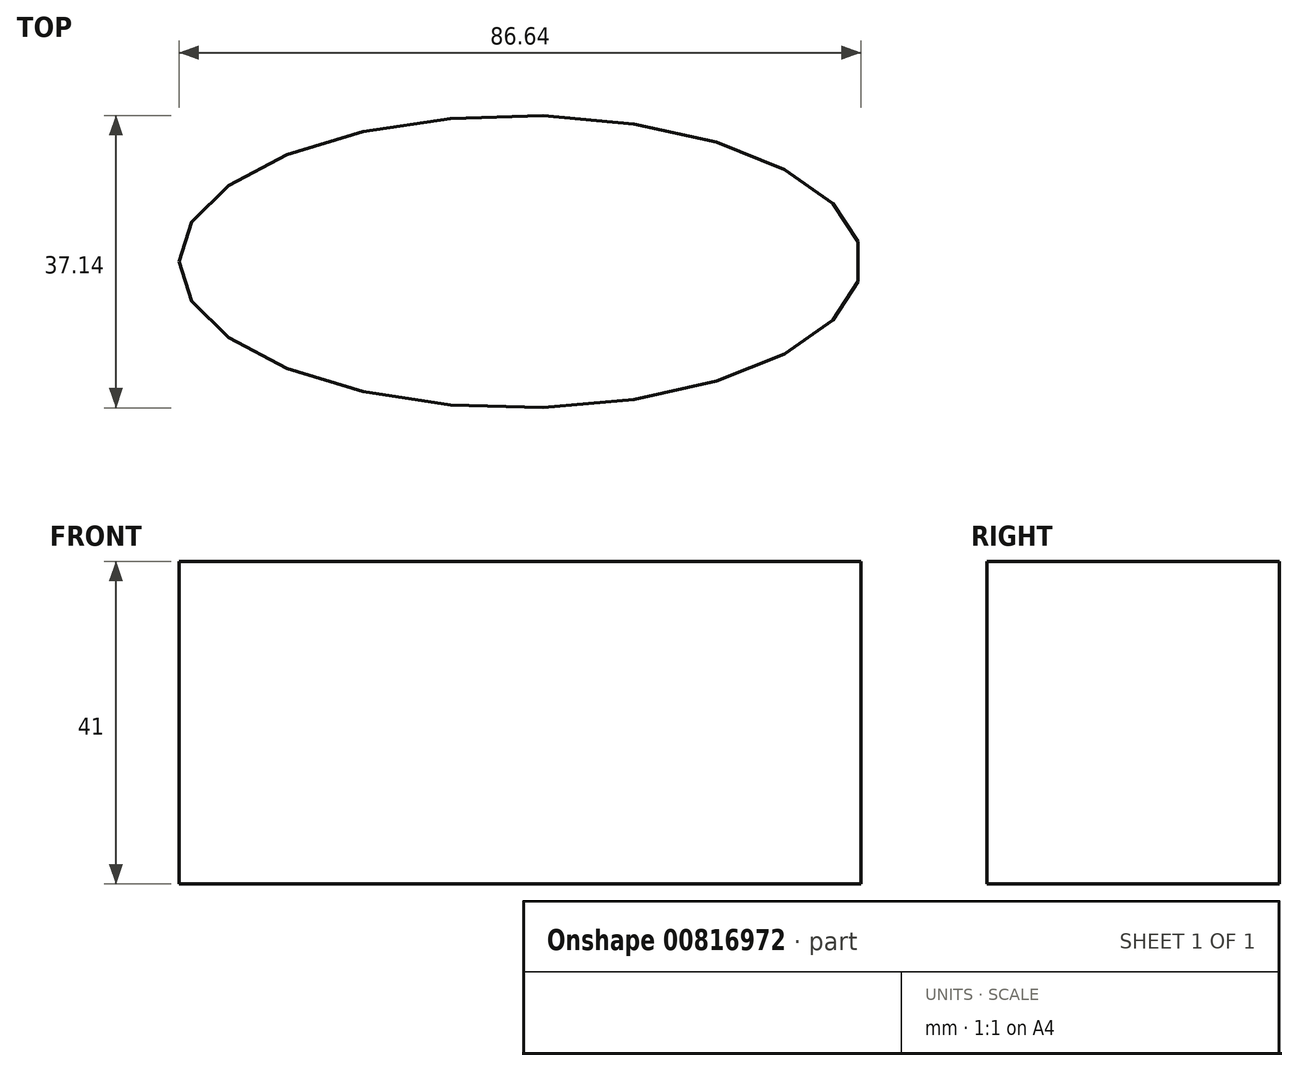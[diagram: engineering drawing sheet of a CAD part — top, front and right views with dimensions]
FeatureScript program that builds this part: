
annotation { "Feature Type Name" : "Feature", "Feature Type Description" : "" }
export const myFeature = defineFeature(function(context is Context, id is Id, definition is map)
    precondition{}
    {
        {
            var Q0;
            Q0=qCreatedBy(makeId("Top.planeOp"),FACE);
            var sketch = newSketch(context, id + "F0", { "sketchPlane" : qUnion([Q0])});
            skEllipse(sketch, "E0", {"center": v(0, 0) * mm, "majorRadius": 43.32 * mm, "minorRadius": 18.57 * mm, "majorAxis": v(-1, 0)});
            skSolve(sketch);
        }
        {
            var Q0;
            Q0 = qSketchRegion(id + "F0", true);
            extrude(context, id + "F1", {"entities" : qUnion([Q0]), "depth" : 41 * mm, "offsetDistance" : 25.4 * mm});
        }
    });
